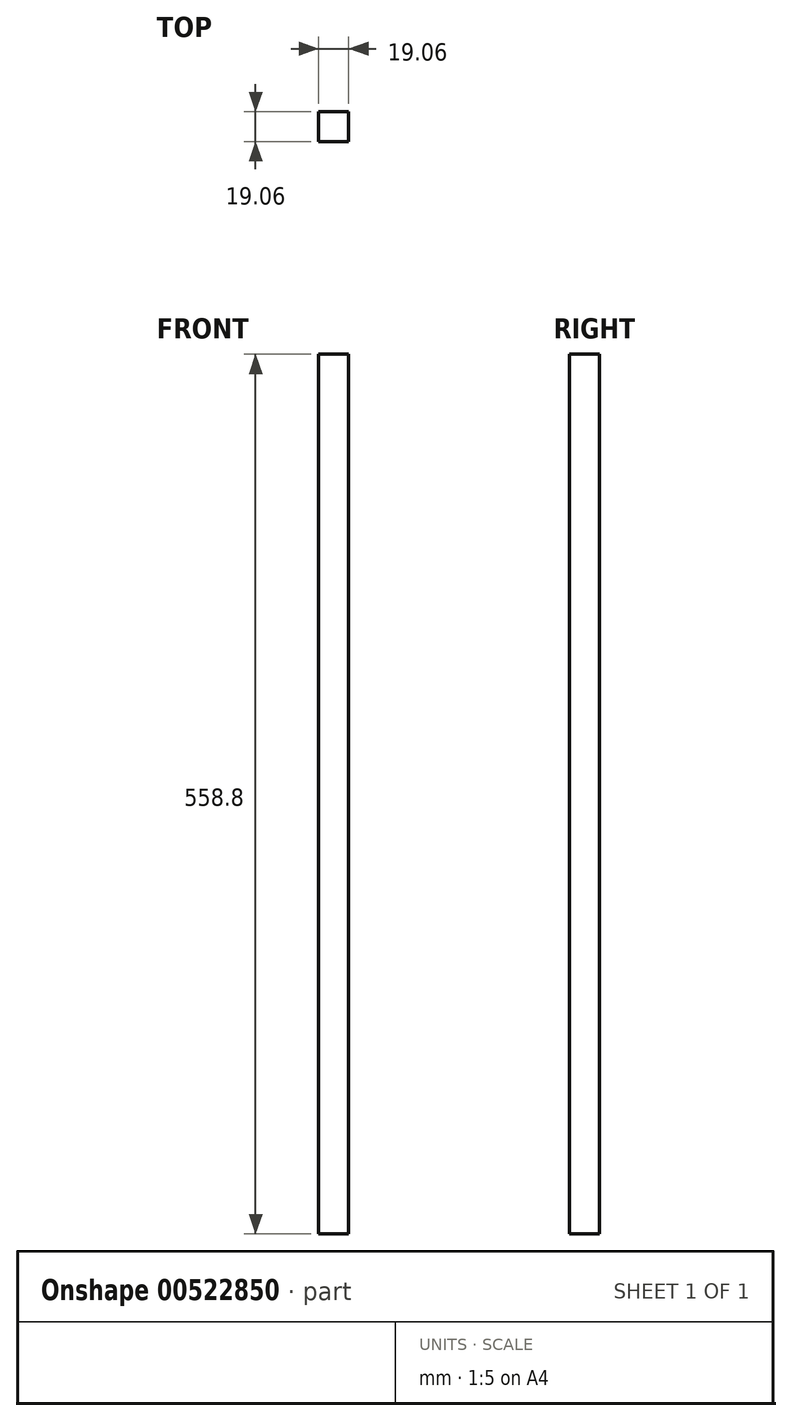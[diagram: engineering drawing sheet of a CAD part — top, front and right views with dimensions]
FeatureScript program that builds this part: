
annotation { "Feature Type Name" : "Feature", "Feature Type Description" : "" }
export const myFeature = defineFeature(function(context is Context, id is Id, definition is map)
    precondition{}
    {
        {
            var Q0;
            Q0=qCreatedBy(makeId("Top.planeOp"),FACE);
            var sketch = newSketch(context, id + "F0", { "sketchPlane" : qUnion([Q0])});
            skLineSegment(sketch, "E0.bottom", {"start": v(-9.52, 9.53) * mm, "end": v(9.53, 9.53) * mm});
            skLineSegment(sketch, "E0.top", {"start": v(-9.53, -9.52) * mm, "end": v(9.52, -9.52) * mm});
            skLineSegment(sketch, "E0.left", {"start": v(-9.52, 9.53) * mm, "end": v(-9.53, -9.52) * mm});
            skLineSegment(sketch, "E0.right", {"start": v(9.53, 9.53) * mm, "end": v(9.53, -9.52) * mm});
            skPoint(sketch, "E0.middle", {"position": v(0, 0) * mm});
            skSolve(sketch);
        }
        {
            var Q0;
            Q0=makeQuery(id+"F0.imprint","IMPRINT",FACE,{"disambiguationData":[TD([[makeQuery(id+"F0.imprint","IMPRINT",EDGE,{"derivedFrom":sQuery(id+"F0.wireOp",EDGE,"E0.bottom")}),-1.0]])]});
            extrude(context, id + "F1", {"entities" : qUnion([Q0]), "depth" : 558.8 * mm, "offsetDistance" : 25.4 * mm});
        }
    });
